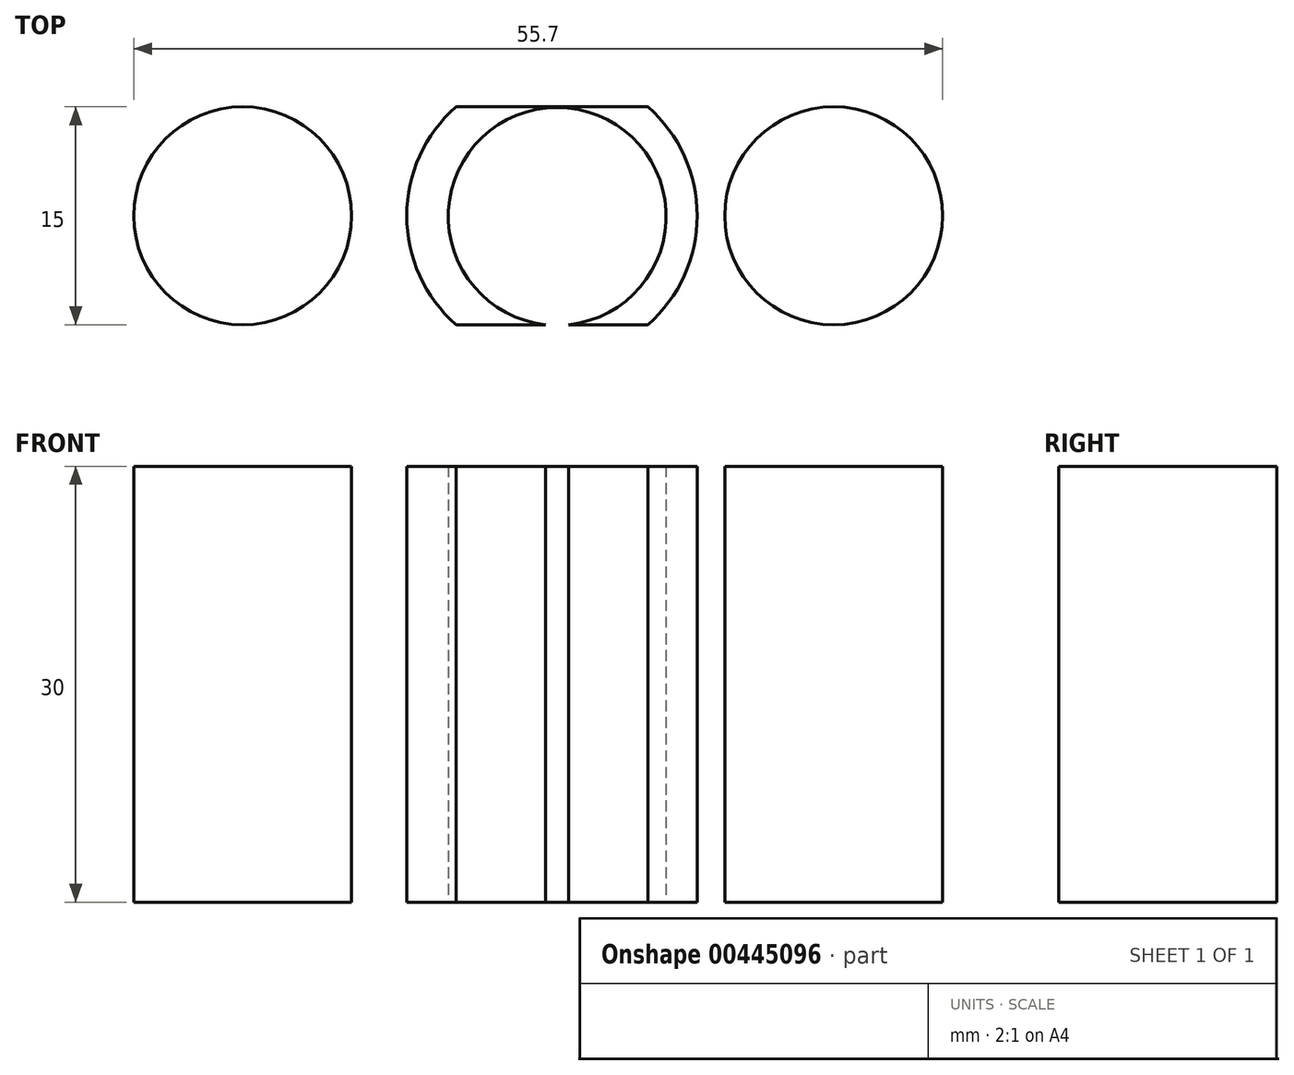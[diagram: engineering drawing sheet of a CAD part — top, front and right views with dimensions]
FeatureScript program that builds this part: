
annotation { "Feature Type Name" : "Feature", "Feature Type Description" : "" }
export const myFeature = defineFeature(function(context is Context, id is Id, definition is map)
    precondition{}
    {
        {
            var Q0;
            Q0=qCreatedBy(makeId("Top.planeOp"),FACE);
            var sketch = newSketch(context, id + "F0", { "sketchPlane" : qUnion([Q0])});
            skLineSegment(sketch, "E0.bottom", {"start": v(32.5, 7.5) * mm, "end": v(-32.5, 7.5) * mm});
            skLineSegment(sketch, "E0.top", {"start": v(32.5, -7.5) * mm, "end": v(-32.5, -7.5) * mm});
            skLineSegment(sketch, "E0.left", {"start": v(32.5, 7.5) * mm, "end": v(32.5, -7.5) * mm});
            skLineSegment(sketch, "E0.right", {"start": v(-32.5, 7.5) * mm, "end": v(-32.5, -7.5) * mm});
            skPoint(sketch, "E0.middle", {"position": v(0, 0) * mm});
            skCircle(sketch, "E1", {"center": v(0, 0) * mm, "radius": 10 * mm});
            skCircle(sketch, "E2", {"center": v(0.36, -0.04) * mm, "radius": 7.5 * mm});
            skCircle(sketch, "E3", {"center": v(-21.3, 0) * mm, "radius": 7.5 * mm});
            skCircle(sketch, "E4", {"center": v(19.4, 0) * mm, "radius": 7.5 * mm});
            skSolve(sketch);
        }
        {
            var Q0;
            {var subQ0=sQuery(id+"F0.wireOp",EDGE,"E4");var subQ1=makeQuery(id+"F0.imprint","INTERSECT",VERTEX,{"derivedFrom":[sQuery(id+"F0.wireOp",EDGE,"E0.bottom"),subQ0]});Q0=makeQuery(id+"F0.imprint","IMPRINT",FACE,{"disambiguationData":[TD([[makeQuery(id+"F0.imprint","IMPRINT",EDGE,{"disambiguationData":[TD([[subQ1,-1.0]])],"derivedFrom":subQ0}),1.0]])]});}
            var Q1;
            {var subQ0=sQuery(id+"F0.wireOp",EDGE,"E3");var subQ1=makeQuery(id+"F0.imprint","INTERSECT",VERTEX,{"derivedFrom":[sQuery(id+"F0.wireOp",EDGE,"E0.bottom"),subQ0]});Q1=makeQuery(id+"F0.imprint","IMPRINT",FACE,{"disambiguationData":[TD([[makeQuery(id+"F0.imprint","IMPRINT",EDGE,{"disambiguationData":[TD([[subQ1,-1.0]])],"derivedFrom":subQ0}),1.0]])]});}
            var Q2;
            {var subQ0=sQuery(id+"F0.wireOp",EDGE,"E2");var subQ1=sQuery(id+"F0.wireOp",EDGE,"E0.top");var subQ2=makeQuery(id+"F0.imprint","INTERSECT",VERTEX,{"disambiguationData":[OD(0.0)],"derivedFrom":[subQ1,subQ0]});Q2=makeQuery(id+"F0.imprint","IMPRINT",FACE,{"disambiguationData":[TD([[makeQuery(id+"F0.imprint","IMPRINT",EDGE,{"disambiguationData":[TD([[subQ2,-1.0]])],"derivedFrom":subQ1}),-1.0]])]});}
            extrude(context, id + "F1", {"entities" : qUnion([Q0, Q1, Q2]), "depth" : 30 * mm});
        }
        {
            var Q0;
            Q0=sQuery(id+"F0.wireOp",EDGE,"E1");
            extrude(context, id + "F2", {"bodyType" : ToolBodyType.SURFACE, "surfaceEntities" : qUnion([Q0]), "oppositeDirection" : true, "depth" : 40 * mm});
        }
        {
            var Q0;
            Q0=sQuery(id+"F0.wireOp",EDGE,"E0.bottom");
            var Q1;
            Q1=sQuery(id+"F0.wireOp",EDGE,"E0.top");
            var Q2;
            Q2=sQuery(id+"F0.wireOp",EDGE,"E0.right");
            var Q3;
            Q3=sQuery(id+"F0.wireOp",EDGE,"E0.left");
            extrude(context, id + "F3", {"bodyType" : ToolBodyType.SURFACE, "surfaceEntities" : qUnion([Q0, Q1, Q2, Q3]), "depth" : 25 * mm});
        }
    });
